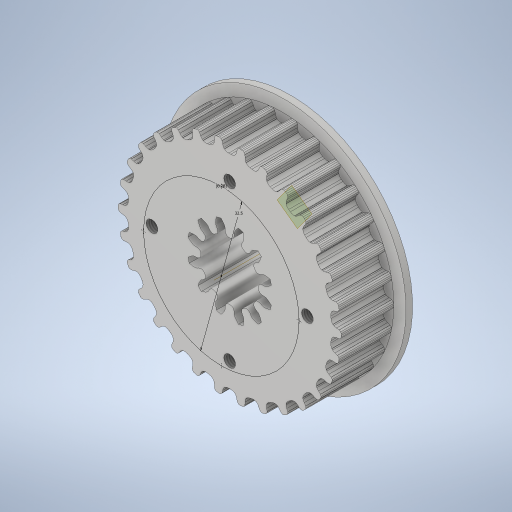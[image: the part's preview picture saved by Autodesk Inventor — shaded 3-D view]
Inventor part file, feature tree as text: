
AUTODESK INVENTOR PART (.ipt)
format: ipt  version: 2023 (Build 270158000, 158)  size: 2,438,656 bytes
history: native  units: in
note: dims shown in document units (in); Inventor stores cm internally (conversion verified against a paired STEP export)
features: extrude x3, sketch x2, mirror x2, hole x2, projected_geometry x2, other x1, boolean_combine x1, plane x1, split x1
ambient origin geometry x8: Origin, YZ Plane, XZ Plane, XY Plane, X Axis, Y Axis, Z Axis, Center Point
bodies: Solid1 (feature_tree), Solid2 (feature_tree), Solid3 (feature_tree), Solid4 (feature_tree)
feature tree (15):
  sketch  "Sketch1"  dims[d0=0.3937in d1=0.0in d2=0.3937in d3=0.0in]
  extrude  "Extrusion1"  Depth=0.3937in TaperAngle=0.0deg
  extrude  "Extrusion2"  Depth=0.3937in TaperAngle=0.0deg
  other  "Cut-Extrude2"
  extrude  "Extrusion3"  Depth=0.3937in
  boolean_combine  "Combine1"
  mirror  "Mirror2"
  sketch  "Sketch3"  dims[d4=0.3937in d5=0.3937in d6=0.0in d7=1.2795in d8=1.5748in d10=360.0deg d12=0.0968in d13=0.2362in d14=0.225in d15=0.075in d16=90.0deg d17=0.315in d18=0.8108in d19=0.0in d20=0.1339in d21=0.2362in d22=0.248in d23=0.0787in d24=0.6181in d25=0.315in d26=0.8108in]
  hole  "Hole1"  [1 undecoded]
  plane  "Work Plane1"
  split  "Split1"
  hole  "Hole2"  [1 undecoded]
  projected_geometry  "Projected Loop1"
  projected_geometry  "Projected Loop2"
  mirror  "Mirror1"
note: 2 required parameter values undecoded (feature->parameter linkage not recoverable at this tier; creation-order binding heuristic only, values carry confidence <= 0.55)
